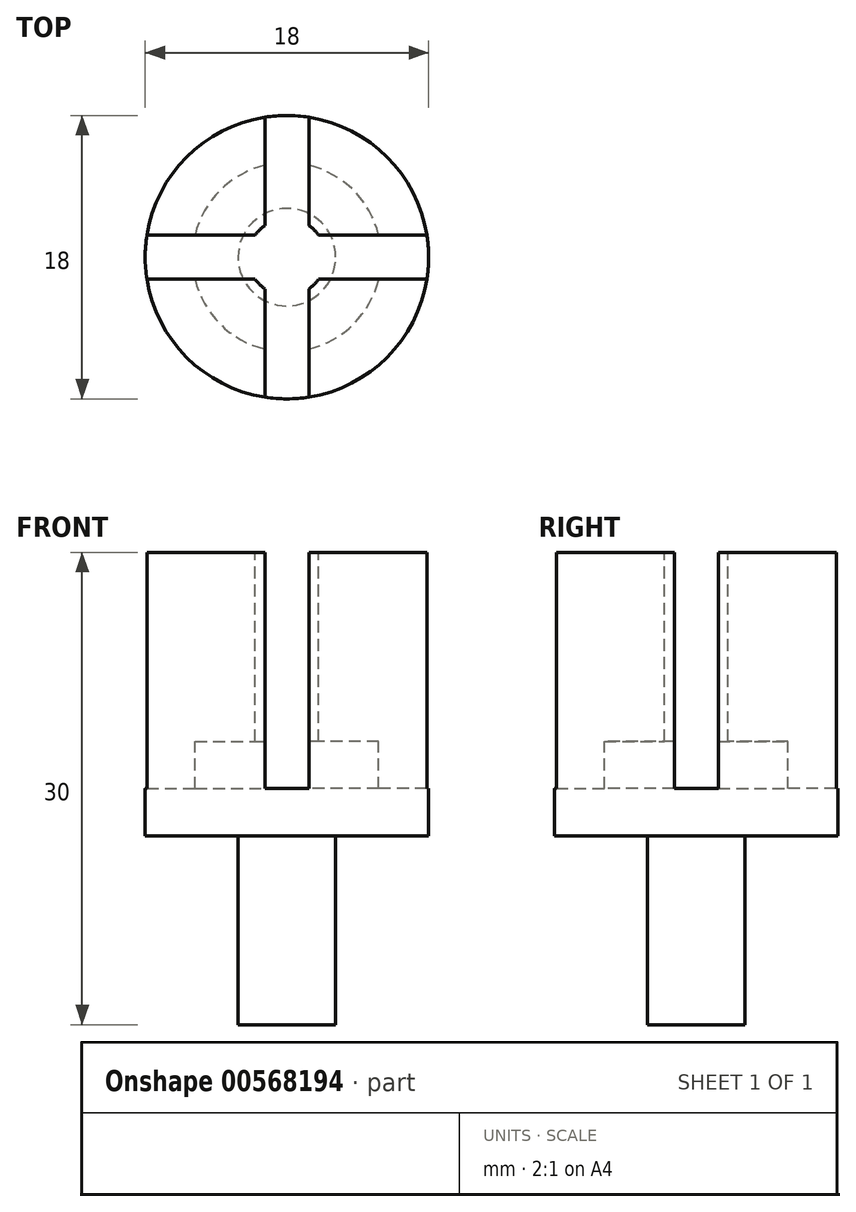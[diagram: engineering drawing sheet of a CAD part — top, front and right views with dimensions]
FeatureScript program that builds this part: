
annotation { "Feature Type Name" : "Feature", "Feature Type Description" : "" }
export const myFeature = defineFeature(function(context is Context, id is Id, definition is map)
    precondition{}
    {
        {
            var Q0;
            Q0=qCreatedBy(makeId("Front.planeOp"),FACE);
            var sketch = newSketch(context, id + "F0", { "sketchPlane" : qUnion([Q0])});
            skLineSegment(sketch, "E0", {"start": v(0, 0) * mm, "end": v(-3.1, 0) * mm});
            skLineSegment(sketch, "E1", {"start": v(-3.1, 0) * mm, "end": v(-3.1, 12) * mm});
            skLineSegment(sketch, "E2", {"start": v(-3.1, 12) * mm, "end": v(-9, 12) * mm});
            skLineSegment(sketch, "E3", {"start": v(-9, 12) * mm, "end": v(-9, 30) * mm});
            skLineSegment(sketch, "E4", {"start": v(-9, 30) * mm, "end": v(-2.45, 30) * mm});
            skLineSegment(sketch, "E5", {"start": v(0, 15) * mm, "end": v(0, 0) * mm});
            skLineSegment(sketch, "E6", {"start": v(-2.45, 30) * mm, "end": v(-2.45, 18) * mm});
            skLineSegment(sketch, "E7", {"start": v(-2.45, 18) * mm, "end": v(-6, 18) * mm});
            skLineSegment(sketch, "E8", {"start": v(-6, 18) * mm, "end": v(-6, 15) * mm});
            skLineSegment(sketch, "E9", {"start": v(-6, 15) * mm, "end": v(0, 15) * mm});
            skSolve(sketch);
        }
        {
            var Q0;
            Q0=qSketchRegion(id+"F0",true);
            var Q1;
            Q1=sQuery(id+"F0.wireOp",EDGE,"E5");
            revolve(context, id + "F1", {"entities" : qUnion([Q0]), "axis" : qUnion([Q1]), "revolveType" : RevolveType.FULL});
        }
        {
            var Q0;
            Q0=makeQuery(id+"F1.opRevolve","SWEPT_FACE",FACE,{"disambiguationData":[OSD([sQuery(id+"F0.wireOp",EDGE,"E4")])]});
            var sketch = newSketch(context, id + "F2", { "sketchPlane" : qUnion([Q0])});
            skLineSegment(sketch, "E10", {"start": v(-1.4, 9) * mm, "end": v(-1.4, 1.7) * mm});
            skLineSegment(sketch, "E11", {"start": v(1.4, 9) * mm, "end": v(1.4, 1.7) * mm});
            skLineSegment(sketch, "E12", {"start": v(-1.4, 1.7) * mm, "end": v(1.4, 1.7) * mm});
            skLineSegment(sketch, "E13.2.0", {"start": v(1.1, -11.1) * mm, "end": v(-1.7, -11.1) * mm});
            skPoint(sketch, "E13.center", {"position": v(0, -1.05) * mm});
            skLineSegment(sketch, "E14.2.0", {"start": v(1.1, -9) * mm, "end": v(-1.7, -9) * mm});
            skPoint(sketch, "E14.center", {"position": v(0, 0) * mm});
            skLineSegment(sketch, "E15", {"start": v(-1.4, 9) * mm, "end": v(1.4, 9) * mm});
            skLineSegment(sketch, "E16.1.0", {"start": v(-9, -1.4) * mm, "end": v(-1.7, -1.4) * mm});
            skLineSegment(sketch, "E16.1.1", {"start": v(-9, -1.4) * mm, "end": v(-9, 1.4) * mm});
            skLineSegment(sketch, "E16.1.2", {"start": v(-9, 1.4) * mm, "end": v(-1.7, 1.4) * mm});
            skLineSegment(sketch, "E16.1.3", {"start": v(-1.7, -1.4) * mm, "end": v(-1.7, 1.4) * mm});
            skLineSegment(sketch, "E16.2.0", {"start": v(1.4, -9) * mm, "end": v(1.4, -1.7) * mm});
            skLineSegment(sketch, "E16.2.1", {"start": v(1.4, -9) * mm, "end": v(-1.4, -9) * mm});
            skLineSegment(sketch, "E16.2.2", {"start": v(-1.4, -9) * mm, "end": v(-1.4, -1.7) * mm});
            skLineSegment(sketch, "E16.2.3", {"start": v(1.4, -1.7) * mm, "end": v(-1.4, -1.7) * mm});
            skLineSegment(sketch, "E16.3.0", {"start": v(9, 1.4) * mm, "end": v(1.7, 1.4) * mm});
            skLineSegment(sketch, "E16.3.1", {"start": v(9, 1.4) * mm, "end": v(9, -1.4) * mm});
            skLineSegment(sketch, "E16.3.2", {"start": v(9, -1.4) * mm, "end": v(1.7, -1.4) * mm});
            skLineSegment(sketch, "E16.3.3", {"start": v(1.7, 1.4) * mm, "end": v(1.7, -1.4) * mm});
            skSolve(sketch);
        }
        {
            var Q0;
            Q0=qSketchRegion(id+"F2",true);
            extrude(context, id + "F3", {"entities" : qUnion([Q0]), "operationType" : NewBodyOperationType.REMOVE, "oppositeDirection" : true, "depth" : 15 * mm, "offsetDistance" : 25 * mm});
        }
    });
